# Revit family: Domotics-DomesticRanges-GEWISS-CHORUS_POWER-SOCKET-OUTLET_FAST_WIRING_FRA
name_source: partatom
category: Apparecchi elettrici
revit_build: Autodesk Revit 2016 (Build: 20161004_0715(x64)
units: mm (PartAtom-declared; Revit-internal decimal feet)

## family parameters
Condiviso = Sì
Host = Superficie
Mantenere orientamento annotazione = Sì
Punto di calcolo locali = Sì
Quota connettore circolare = Usa diametro
Taglio con vuoti quando caricato = Sì
Tipo di parte = Normale

## types (4) — shared parameters
Breaking capacity: = 1.25 In (100 position changes)
Carico apparente = 0 VA
Catalogue = DOMOTICS
Catalogue Range = CHORUS - DOMESTIC RANGE
Category = Socket-outlet
Characteristics = With safety shields
Description. = Socket-outlet
Description: = 2P+E - 16A
Electrocod = 0131
For plug pins = Ã˜ 4 / 4.8 mm
Glow Wire Test = 850°C
IDF = bada8f19-9650-48be-b998-9467c3396dc6
IDT = a90b3aa5-a732-4d85-b430-486886653f2e
Immagine tipo = GW14247F.jpg
Insulation resistance = > 5 MOhm
N. poli = 1
No. Chorus modules = 2
No. Chorus modules: = 2
Produttore = GEWISS S.p.A.
Prolonged operation (no.of position changes) = 10.000 at In 250 V ac cosÃ˜=0,8
Prospetto di default = 1219 mm
Resistance at test voltage = 2000 V at 50 Hz for 1 minute
SEO = Socket outlet
Standard = French
Standard: = French
Standard; = IEC 60884-1; NF C 61-314
TXT ELETTRICO = 16
Technical sheet = https://www.gewiss.com
Terminal grip on cable traction = > 50 N
Terminal tightening capacity flexible cables (mm2) = min. 0,75 - max. 2x4
Terminal tightening capacity rigid cables (mm2) = min. 0,5 - max. 2x2,5
Thermo-pressure with ball = 125
Tipo_ = Chorus Prese Fra_GENERICO : GW14247F Presa 2M 2P+T 16A cabl. rapido standard Francese titanio
URL = https://www.gewiss.com
Version file RFA = 19.0
Volt = 230 V
Voltage = 250 V ac
Voltage: = 250 V ac
Wiring terminals = Quick, with spring

## per-type parameters (varying)
| type | Colour | Descrizione | EAN code | Modello | Type | Type: |
| GW10247F - Socket outlet 2M 2P+E 16A fr quick wiring wh | White | S. OUTL. 2M 2P+E 16A FR QUICK WIRING WH | 8011564425309 | GW10247F | Quick wiring |  |
| GW10257F - Socket outlet 2M 2P+E 16A fr quick wiring red | Red | S. OUTL. 2M 2P+E 16A FR QUICK WIRING RED | 8011564264984 | GW10257F | For allocated lines | For allocated lines |
| GW14247F - Socket outlet 2M 2P+E 16A french o.q.wir.titan. | Titanium | 2M 2P+E 16A FRENCH SOCKET O.Q.WIR.TITAN. | 8011564266391 | GW14247F | Quick wiring |  |
| GW12247F - Socket outlet 2M 2P+E 16A french o.q.wir.black | Black | 2M 2P+E 16A FRENCH SOCKET O.Q.WIR.BLACK | 8011564268845 | GW12247F | Quick wiring |  |

note: source unit labels omitted for Thermo-pressure with ball — the stored unit's dimension contradicts the parameter name (converter mislabeling)

## geometry (parser evidence)
native form markers: Sweep x1
no freeform markers — native parametric forms only
